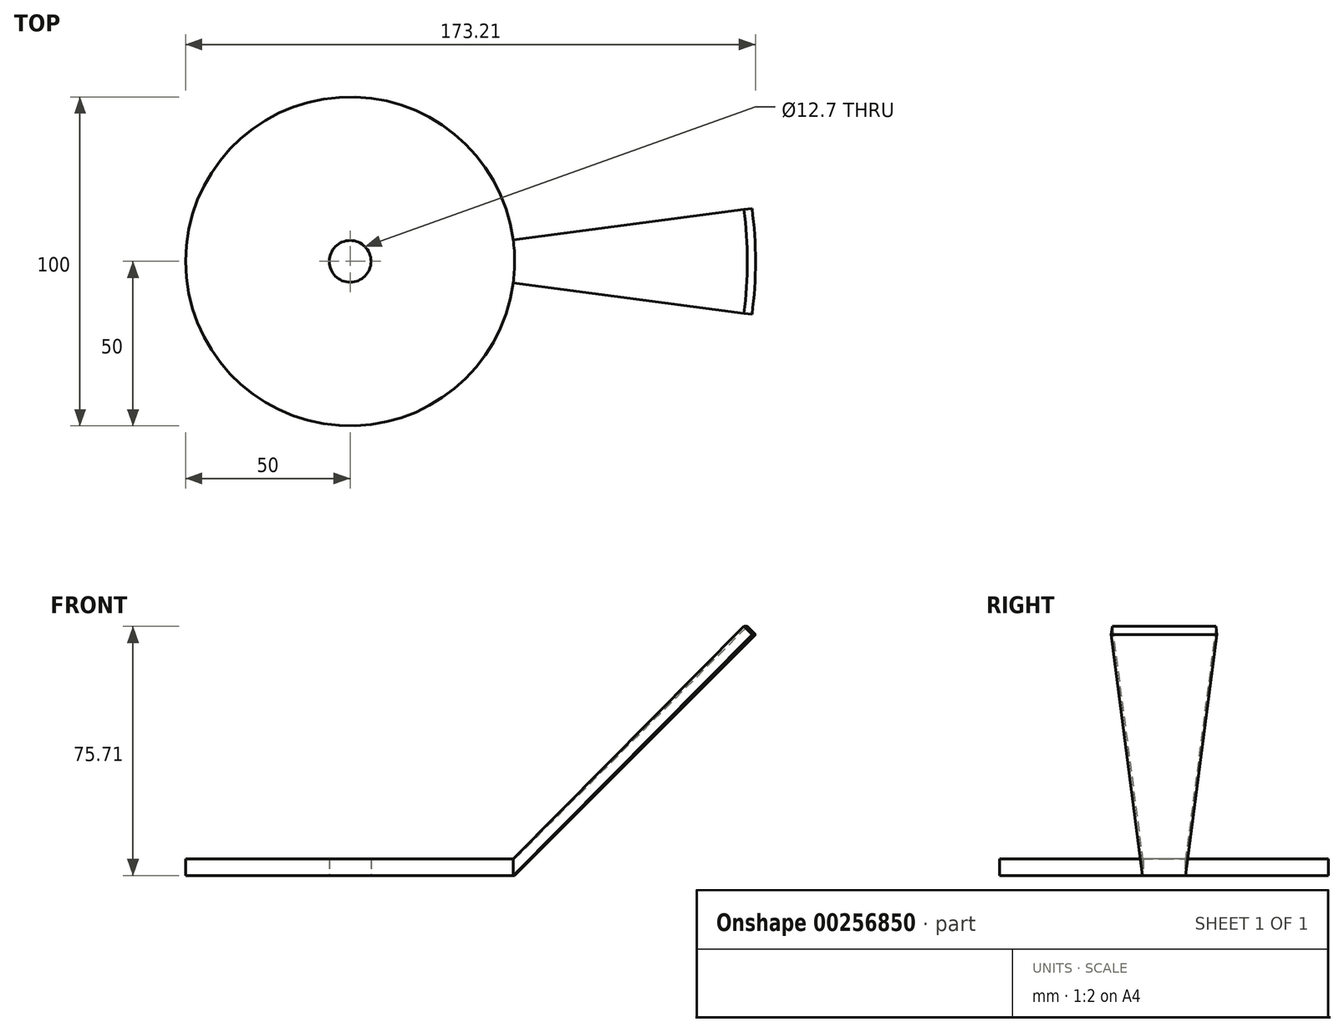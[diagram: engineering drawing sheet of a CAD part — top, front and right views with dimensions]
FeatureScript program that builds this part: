
annotation { "Feature Type Name" : "Feature", "Feature Type Description" : "" }
export const myFeature = defineFeature(function(context is Context, id is Id, definition is map)
    precondition{}
    {
        {
            var Q0;
            Q0=qCreatedBy(makeId("Top.planeOp"),FACE);
            var sketch = newSketch(context, id + "F0", { "sketchPlane" : qUnion([Q0])});
            skCircle(sketch, "E0", {"center": v(0, 0) * mm, "radius": 50 * mm});
            skCircle(sketch, "E1", {"center": v(0, 0) * mm, "radius": 6.35 * mm});
            skSolve(sketch);
        }
        {
            var Q0;
            Q0=makeQuery(id+"F0.imprint","IMPRINT",FACE,{"disambiguationData":[TD([[makeQuery(id+"F0.imprint","IMPRINT",EDGE,{"derivedFrom":sQuery(id+"F0.wireOp",EDGE,"E0")}),1.0]])]});
            extrude(context, id + "F1", {"entities" : qUnion([Q0]), "depth" : 5 * mm});
        }
        {
            var Q0;
            Q0=qCreatedBy(makeId("Front.planeOp"),FACE);
            var sketch = newSketch(context, id + "F2", { "sketchPlane" : qUnion([Q0])});
            skLineSegment(sketch, "E2", {"start": v(-50, 0) * mm, "end": v(-50, 5) * mm});
            skLineSegment(sketch, "E3", {"start": v(50, 5) * mm, "end": v(50, 0) * mm});
            skLineSegment(sketch, "E4", {"start": v(50, 0) * mm, "end": v(123.21, 73.21) * mm});
            skLineSegment(sketch, "E5", {"start": v(123.21, 73.21) * mm, "end": v(120.71, 75.71) * mm});
            skLineSegment(sketch, "E6", {"start": v(120.71, 75.71) * mm, "end": v(50, 5) * mm});
            skLineSegment(sketch, "E7", {"start": v(0, -1.68) * mm, "end": v(0, 24.53) * mm});
            skSolve(sketch);
        }
        {
            var Q0;
            Q0=makeQuery(id+"F2.imprint","IMPRINT",FACE,{"disambiguationData":[TD([[makeQuery(id+"F2.imprint","IMPRINT",EDGE,{"derivedFrom":sQuery(id+"F2.wireOp",EDGE,"E3")}),1.0]])]});
            var Q1;
            Q1=sQuery(id+"F2.wireOp",EDGE,"E7");
            revolve(context, id + "F3", {"operationType" : NewBodyOperationType.ADD, "entities" : qUnion([Q0]), "axis" : qUnion([Q1]), "revolveType" : RevolveType.SYMMETRIC, "angle" : 15 * degree});
        }
    });
